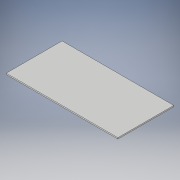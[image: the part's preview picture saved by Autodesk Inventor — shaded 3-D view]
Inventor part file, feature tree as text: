
AUTODESK INVENTOR PART (.ipt)
format: ipt  version: 2019.4 (Build 234330000, 330)  size: 89,088 bytes
history: native  units: mm
features: other x1, extrude x1, sketch x1
ambient origin geometry x8: Origin, YZ Plane, XZ Plane, XY Plane, X Axis, Y Axis, Z Axis, Center Point
bodies: Body1 (feature_tree)
feature tree (3):
  other  "ソリッド1"
  extrude  "押し出し1"  Depth=180.0mm
  sketch  "スケッチ1"
